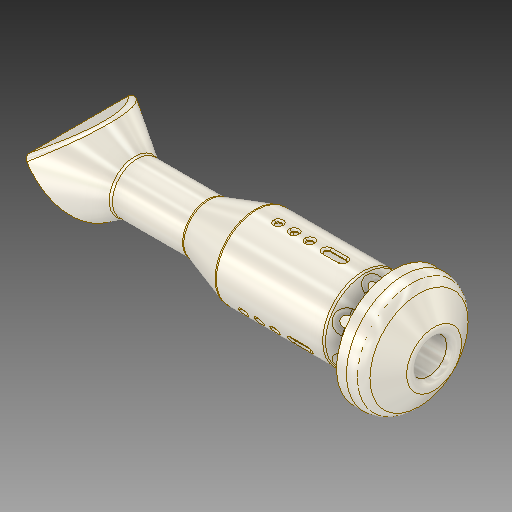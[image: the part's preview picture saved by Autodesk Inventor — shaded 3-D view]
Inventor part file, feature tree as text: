
AUTODESK INVENTOR PART (.ipt)
format: ipt  version: 2019 (Build 230136000, 136)  size: 878,080 bytes
history: native  units: mm
features: sketch x6, fillet x5, plane x5, extrude x3, split x2, pattern_circular x2, revolve x1, projected_geometry x1
ambient origin geometry x8: Origin, YZ Plane, XZ Plane, XY Plane, X Axis, Y Axis, Z Axis, Center Point
bodies: Solid3 (feature_tree)
feature tree (25):
  revolve  "Revolution1"  [1 undecoded]
  fillet  "Fillet1"  Radius=15.925mm
  fillet  "Fillet2"  Radius=28.291787mm
  plane  "Work Plane1"
  plane  "Work Plane3"
  sketch  "Sketch2"  dims[d29=34.13mm d30=13.486mm d31=26.455701mm]
  plane  "Work Plane4"
  sketch  "Sketch3"  dims[d32=12.816mm d33=15.343mm d34=9.609783mm]
  plane  "Work Plane5"
  split  "Split1"
  split  "Split2"
  extrude  "Extrusion1"  Depth=13.486mm
  fillet  "Fillet3"  Radius=26.455701mm
  plane  "Work Plane6"
  extrude  "Extrusion3"  Depth=15.343mm
  fillet  "Fillet5"  Radius=9.609783mm
  pattern_circular  "Circular Pattern2"  [2 undecoded]
  extrude  "Extrusion4"  Depth=0.8mm
  fillet  "Fillet6"  Radius=5.585054mm
  pattern_circular  "Circular Pattern3"  [2 undecoded]
  sketch  "Sketch1"  dims[d24=6.661mm d26=23.162mm d27=15.925mm d28=28.291787mm]
  sketch  "Sketch4"  dims[d35=6.267mm]
  sketch  "Sketch7"  dims[d36=7.134mm]
  sketch  "Sketch8"  dims[d38=10.52mm d41=1.994mm d42=0.8mm d43=5.585054mm d44=0.8mm d46=0.3mm d48=20.345303mm d49=0.8mm d50=90.0deg d51=1.5mm d52=6.0mm d53=16.0mm d54=5.585054mm d56=21.488mm d57=34.926mm d58=90.0deg d61=0.8mm d62=0.0mm d63=1.4mm d73=6.0mm d74=6.0mm d75=1.5mm d76=10.0mm d77=0.0mm d78=60.0mm d79=360.0deg d81=2.0mm d82=2.0mm d83=30.0mm d85=5.0mm d86=10.0mm d88=10.0mm d90=8.0mm d91=5.0mm d92=1.0mm d93=10.0mm d94=0.0mm d95=0.5mm d96=30.0mm d97=360.0deg]
  projected_geometry  "Project Cut Edges2"
note: 5 required parameter values undecoded (feature->parameter linkage not recoverable at this tier; creation-order binding heuristic only, values carry confidence <= 0.55)